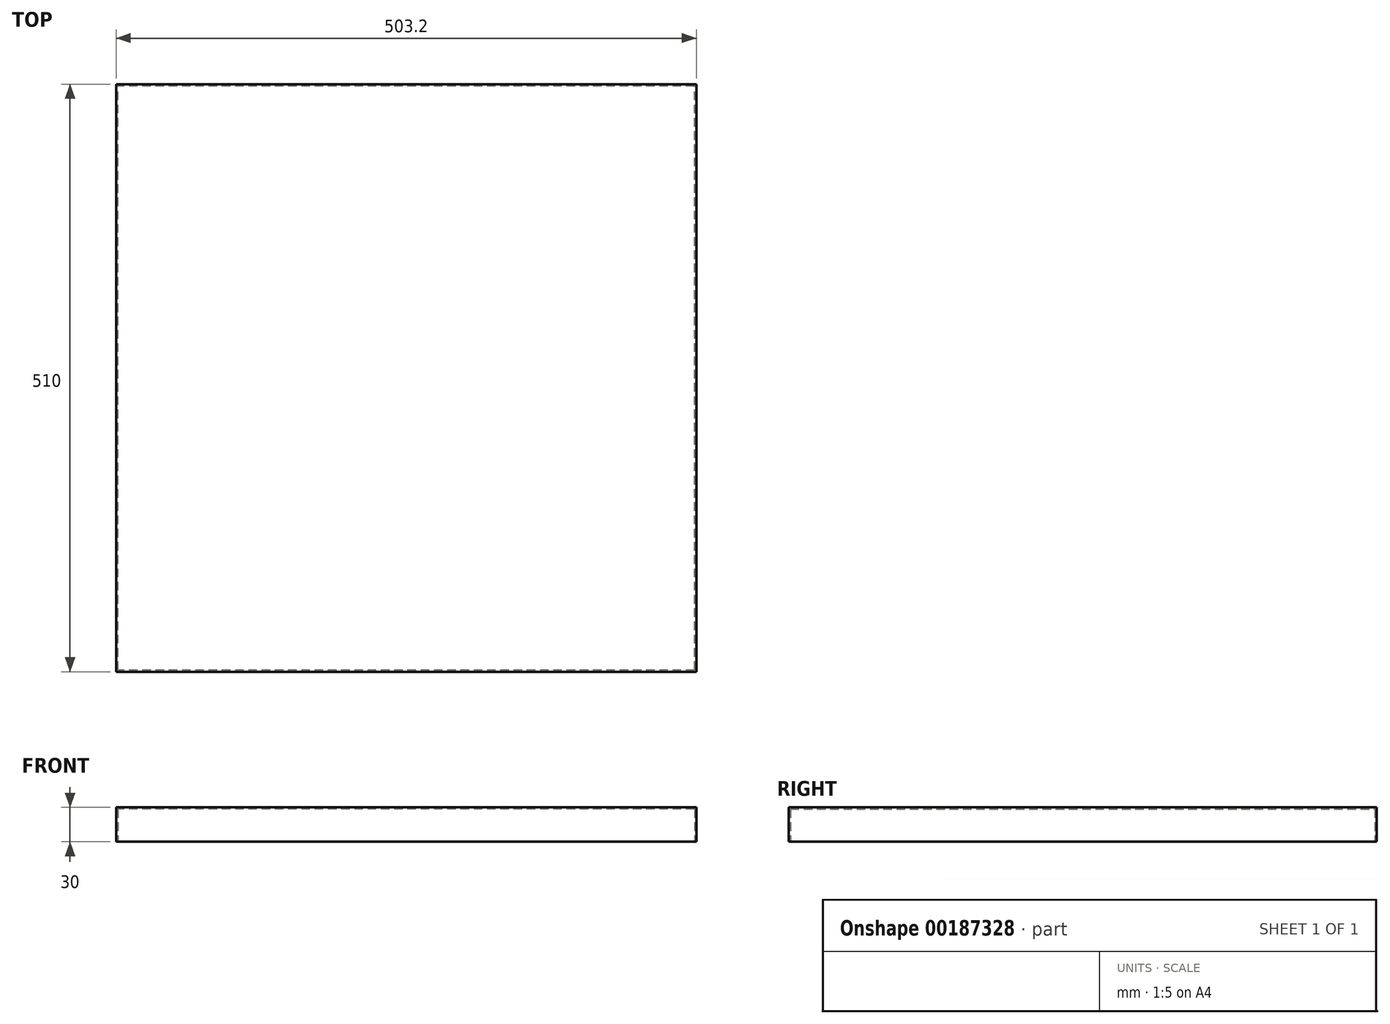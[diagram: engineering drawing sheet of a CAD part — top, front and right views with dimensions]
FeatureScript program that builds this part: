
annotation { "Feature Type Name" : "Feature", "Feature Type Description" : "" }
export const myFeature = defineFeature(function(context is Context, id is Id, definition is map)
    precondition{}
    {
        {
            var Q0;
            Q0=qCreatedBy(makeId("Top.planeOp"),FACE);
            var sketch = newSketch(context, id + "F0", { "sketchPlane" : qUnion([Q0])});
            skLineSegment(sketch, "E0.bottom", {"start": v(251.6, -255) * mm, "end": v(-251.6, -255) * mm});
            skLineSegment(sketch, "E0.top", {"start": v(251.6, 255) * mm, "end": v(-251.6, 255) * mm});
            skLineSegment(sketch, "E0.left", {"start": v(251.6, -255) * mm, "end": v(251.6, 255) * mm});
            skLineSegment(sketch, "E0.right", {"start": v(-251.6, -255) * mm, "end": v(-251.6, 255) * mm});
            skPoint(sketch, "E0.middle", {"position": v(0, 0) * mm});
            skSolve(sketch);
        }
        {
            var Q0;
            Q0 = qSketchRegion(id + "F0", true);
            extrude(context, id + "F1", {"entities" : qUnion([Q0]), "depth" : 30 * mm});
        }
        {
            var Q0;
            Q0=makeQuery(id+"F1.opExtrude","CAP_FACE",FACE,{"disambiguationData":[OSD([sQuery(id+"F0.wireOp",EDGE,"E0.bottom"),sQuery(id+"F0.wireOp",EDGE,"E0.top"),sQuery(id+"F0.wireOp",EDGE,"E0.left"),sQuery(id+"F0.wireOp",EDGE,"E0.right")])],"isStart":true});
            shell(context, id + "F2", {"entities" : qUnion([Q0]), "thickness" : 1.6 * mm});
        }
    });
